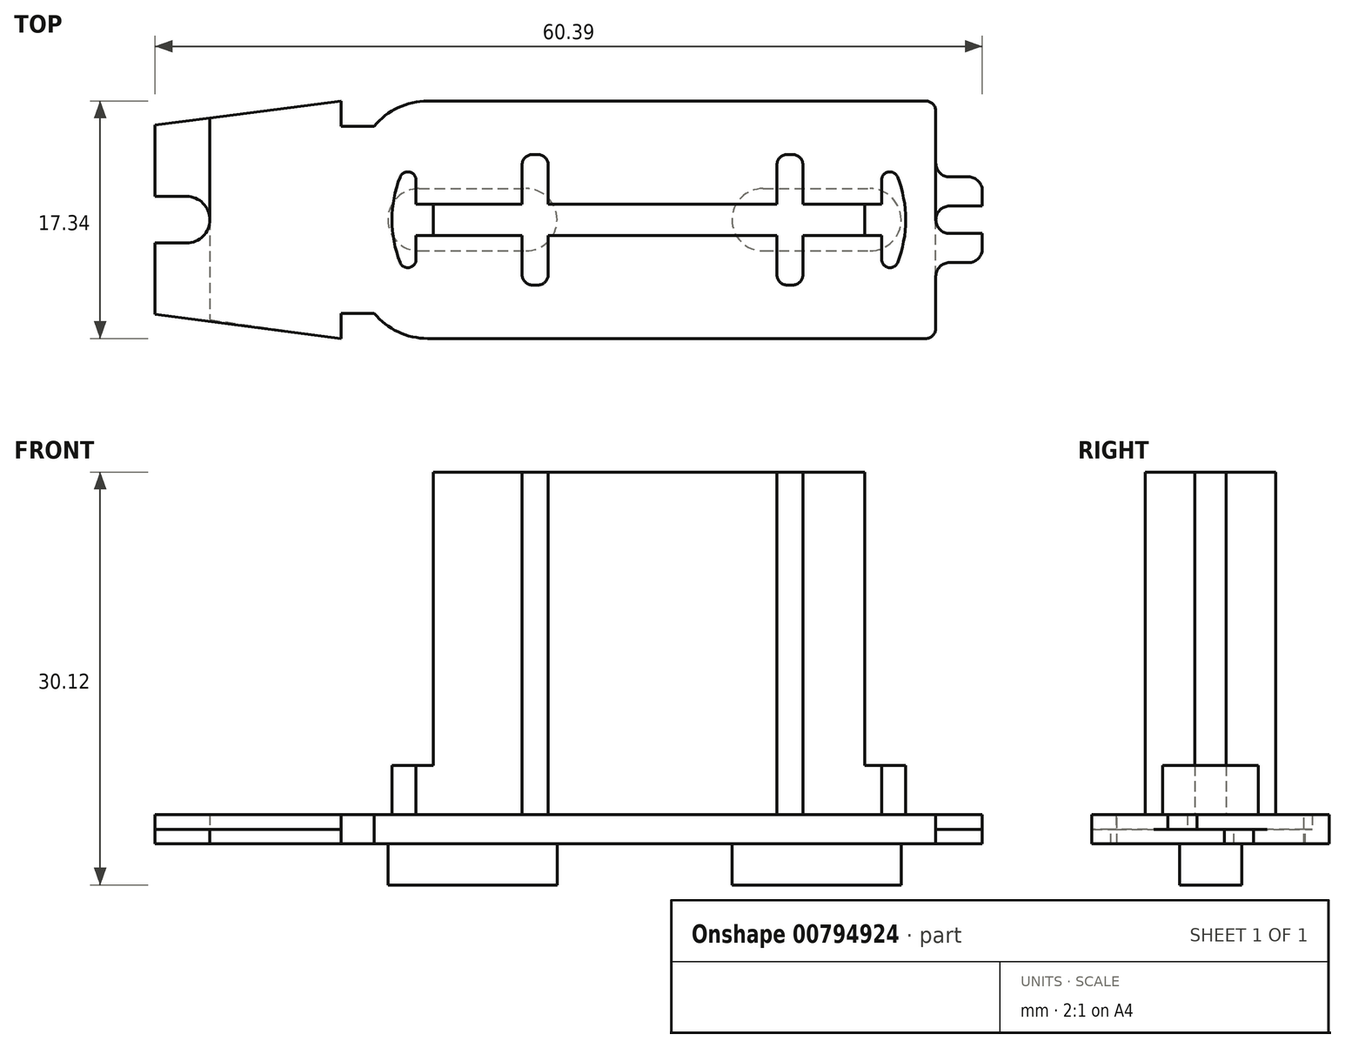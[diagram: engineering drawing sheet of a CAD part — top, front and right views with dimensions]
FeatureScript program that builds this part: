
annotation { "Feature Type Name" : "Feature", "Feature Type Description" : "" }
export const myFeature = defineFeature(function(context is Context, id is Id, definition is map)
    precondition{}
    {
        {
            var Q0;
            Q0=qCreatedBy(makeId("Top.planeOp"),FACE);
            var sketch = newSketch(context, id + "F0", { "sketchPlane" : qUnion([Q0])});
            skLineSegment(sketch, "E0.bottom", {"start": v(-37.1, -8.67) * mm, "end": v(-0.75, -8.67) * mm});
            skLineSegment(sketch, "E0.top", {"start": v(-37.1, 8.67) * mm, "end": v(-0.75, 8.67) * mm});
            skLineSegment(sketch, "E0.right", {"start": v(0, -7.92) * mm, "end": v(0, 0) * mm});
            skLineSegment(sketch, "E1.bottom", {"start": v(1, 3.13) * mm, "end": v(2.39, 3.13) * mm});
            skLineSegment(sketch, "E1.top", {"start": v(1, 1) * mm, "end": v(3.4, 1) * mm});
            skLineSegment(sketch, "E1.right", {"start": v(3.39, 2.12) * mm, "end": v(3.39, 1) * mm});
            skPoint(sketch, "E2.visualSharp", {"position": v(3.39, 3.13) * mm});
            skArc(sketch, "E2.filletArc", {"start": v(3.39, 2.12) * mm, "mid": v(3.1, 2.83) * mm, "end": v(2.39, 3.12) * mm});
            skLineSegment(sketch, "E3.trimOffspring", {"start": v(0, 4.12) * mm, "end": v(0, 7.92) * mm});
            skPoint(sketch, "E4.visualSharp", {"position": v(0, 1) * mm});
            skArc(sketch, "E4.filletArc", {"start": v(1, 1) * mm, "mid": v(0.3, 0.71) * mm, "end": v(0, 0) * mm});
            skPoint(sketch, "E5.visualSharp", {"position": v(0, 3.13) * mm});
            skArc(sketch, "E5.filletArc", {"start": v(0, 4.12) * mm, "mid": v(0.3, 3.42) * mm, "end": v(1, 3.12) * mm});
            skPoint(sketch, "E6.visualSharp", {"position": v(0, 8.67) * mm});
            skArc(sketch, "E6.filletArc", {"start": v(0, 7.92) * mm, "mid": v(-0.22, 8.45) * mm, "end": v(-0.75, 8.67) * mm});
            skPoint(sketch, "E7.visualSharp", {"position": v(0, -8.67) * mm});
            skArc(sketch, "E7.filletArc", {"start": v(-0.75, -8.67) * mm, "mid": v(-0.22, -8.45) * mm, "end": v(0, -7.92) * mm});
            skLineSegment(sketch, "E8.bottom", {"start": v(-41, 6.82) * mm, "end": v(-43.4, 6.82) * mm});
            skLineSegment(sketch, "E8.top", {"start": v(-41, -6.83) * mm, "end": v(-43.4, -6.83) * mm});
            skArc(sketch, "E9", {"start": v(-37.1, 8.67) * mm, "mid": v(-39.26, 8.18) * mm, "end": v(-41, 6.83) * mm});
            skArc(sketch, "E10.MirrorC", {"start": v(-37.1, -8.67) * mm, "mid": v(-39.26, -8.18) * mm, "end": v(-41, -6.82) * mm});
            skLineSegment(sketch, "E11.right", {"start": v(-57, 6.9) * mm, "end": v(-57, 1.7) * mm});
            skLineSegment(sketch, "E12.trimOffspring", {"start": v(-43.4, -6.83) * mm, "end": v(-43.4, -8.66) * mm});
            skLineSegment(sketch, "E13", {"start": v(-43.4, 8.67) * mm, "end": v(-43.4, 6.82) * mm});
            skLineSegment(sketch, "E14", {"start": v(-53, 0) * mm, "end": v(-53, -7.29) * mm});
            skLineSegment(sketch, "E15", {"start": v(-53, -7.29) * mm, "end": v(-43.4, -8.66) * mm});
            skLineSegment(sketch, "E16", {"start": v(-43.4, 8.67) * mm, "end": v(-57, 6.9) * mm});
            skLineSegment(sketch, "E17", {"start": v(-57, 1.7) * mm, "end": v(-54.7, 1.7) * mm});
            skArc(sketch, "E18", {"start": v(-53, 0) * mm, "mid": v(-53.5, 1.2) * mm, "end": v(-54.7, 1.7) * mm});
            skSolve(sketch);
        }
        {
            var Q0;
            Q0 = qSketchRegion(id + "F0", true);
            extrude(context, id + "F1", {"entities" : qUnion([Q0]), "oppositeDirection" : true, "depth" : 1.06 * mm, "offsetDistance" : 25 * mm});
        }
        {
            var Q0;
            Q0=makeQuery(id+"F1.opExtrude","CAP_FACE",FACE,{"disambiguationData":[OSD([sQuery(id+"F0.wireOp",EDGE,"E0.bottom"),sQuery(id+"F0.wireOp",EDGE,"E0.top"),sQuery(id+"F0.wireOp",EDGE,"E0.right"),sQuery(id+"F0.wireOp",EDGE,"E1.bottom"),sQuery(id+"F0.wireOp",EDGE,"E1.top"),sQuery(id+"F0.wireOp",EDGE,"E1.right"),sQuery(id+"F0.wireOp",EDGE,"E2.filletArc"),sQuery(id+"F0.wireOp",EDGE,"E3.trimOffspring"),sQuery(id+"F0.wireOp",EDGE,"E4.filletArc"),sQuery(id+"F0.wireOp",EDGE,"E5.filletArc"),sQuery(id+"F0.wireOp",EDGE,"E6.filletArc"),sQuery(id+"F0.wireOp",EDGE,"E7.filletArc"),sQuery(id+"F0.wireOp",EDGE,"E8.bottom"),sQuery(id+"F0.wireOp",EDGE,"E8.top"),sQuery(id+"F0.wireOp",EDGE,"E9"),sQuery(id+"F0.wireOp",EDGE,"E10.MirrorC"),sQuery(id+"F0.wireOp",EDGE,"E11.right"),sQuery(id+"F0.wireOp",EDGE,"E12.trimOffspring"),sQuery(id+"F0.wireOp",EDGE,"E13"),sQuery(id+"F0.wireOp",EDGE,"E14"),sQuery(id+"F0.wireOp",EDGE,"E15"),sQuery(id+"F0.wireOp",EDGE,"E16"),sQuery(id+"F0.wireOp",EDGE,"E17"),sQuery(id+"F0.wireOp",EDGE,"E18")])],"isStart":true});
            var sketch = newSketch(context, id + "F2", { "sketchPlane" : qUnion([Q0])});
            skArc(sketch, "E19.MirrorCS", {"start": v(-0.75, 8.67) * mm, "mid": v(-0.22, 8.45) * mm, "end": v(0, 7.92) * mm});
            skArc(sketch, "E20.MirrorCS", {"start": v(0, -7.92) * mm, "mid": v(-0.22, -8.45) * mm, "end": v(-0.75, -8.67) * mm});
            skArc(sketch, "E21.MirrorCS", {"start": v(0, -4.12) * mm, "mid": v(0.3, -3.42) * mm, "end": v(1, -3.12) * mm});
            skLineSegment(sketch, "E22.MirrorCS", {"start": v(0, -4.12) * mm, "end": v(0, -7.92) * mm});
            skArc(sketch, "E23.MirrorCS", {"start": v(3.4, -2.12) * mm, "mid": v(3.1, -2.83) * mm, "end": v(2.4, -3.12) * mm});
            skLineSegment(sketch, "E24.MirrorCS", {"start": v(3.4, -2.12) * mm, "end": v(3.4, -1) * mm});
            skLineSegment(sketch, "E25.MirrorCS", {"start": v(1, -1) * mm, "end": v(3.4, -1) * mm});
            skLineSegment(sketch, "E26.MirrorCS", {"start": v(1, -3.12) * mm, "end": v(2.4, -3.12) * mm});
            skLineSegment(sketch, "E27.MirrorCS", {"start": v(-43.4, -8.66) * mm, "end": v(-43.4, -6.83) * mm});
            skLineSegment(sketch, "E28.MirrorCS", {"start": v(-57, -1.7) * mm, "end": v(-54.7, -1.7) * mm});
            skLineSegment(sketch, "E29.MirrorCS", {"start": v(-41, -6.83) * mm, "end": v(-43.4, -6.83) * mm});
            skArc(sketch, "E30.MirrorCS", {"start": v(1, -1) * mm, "mid": v(0.3, -0.71) * mm, "end": v(0, 0) * mm});
            skArc(sketch, "E31.MirrorCS", {"start": v(-37.1, 8.67) * mm, "mid": v(-39.26, 8.18) * mm, "end": v(-41, 6.82) * mm});
            skArc(sketch, "E32.MirrorCS", {"start": v(-37.1, -8.67) * mm, "mid": v(-39.26, -8.18) * mm, "end": v(-41, -6.82) * mm});
            skLineSegment(sketch, "E33.MirrorCS", {"start": v(-41, 6.82) * mm, "end": v(-43.4, 6.82) * mm});
            skLineSegment(sketch, "E34.MirrorCS", {"start": v(-43.4, 6.82) * mm, "end": v(-43.4, 8.67) * mm});
            skArc(sketch, "E35.MirrorCS", {"start": v(-53, 0) * mm, "mid": v(-53.5, -1.2) * mm, "end": v(-54.7, -1.7) * mm});
            skLineSegment(sketch, "E36.MirrorCS", {"start": v(-53, 0) * mm, "end": v(-53, 7.42) * mm});
            skLineSegment(sketch, "E37.MirrorCS", {"start": v(0, 7.91) * mm, "end": v(0, 0) * mm});
            skLineSegment(sketch, "E38.MirrorCS", {"start": v(-37.1, -8.67) * mm, "end": v(-0.75, -8.67) * mm});
            skLineSegment(sketch, "E39.MirrorCS", {"start": v(-37.1, 8.67) * mm, "end": v(-0.75, 8.67) * mm});
            skLineSegment(sketch, "E40.MirrorCS", {"start": v(-43.4, -8.67) * mm, "end": v(-57, -6.9) * mm});
            skLineSegment(sketch, "E41.MirrorCS", {"start": v(-57, -6.9) * mm, "end": v(-57, -1.7) * mm});
            skLineSegment(sketch, "E42.MirrorCS", {"start": v(-53, 7.42) * mm, "end": v(-43.4, 8.67) * mm});
            skSolve(sketch);
        }
        {
            var Q0;
            Q0 = qSketchRegion(id + "F2", true);
            extrude(context, id + "F3", {"entities" : qUnion([Q0]), "operationType" : NewBodyOperationType.ADD, "depth" : 1.06 * mm, "offsetDistance" : 25 * mm});
        }
        {
            var Q0;
            Q0=makeQuery(id+"F1.opExtrude","CAP_FACE",FACE,{"disambiguationData":[OSD([sQuery(id+"F0.wireOp",EDGE,"E0.bottom"),sQuery(id+"F0.wireOp",EDGE,"E0.top"),sQuery(id+"F0.wireOp",EDGE,"E0.right"),sQuery(id+"F0.wireOp",EDGE,"E1.bottom"),sQuery(id+"F0.wireOp",EDGE,"E1.top"),sQuery(id+"F0.wireOp",EDGE,"E1.right"),sQuery(id+"F0.wireOp",EDGE,"E2.filletArc"),sQuery(id+"F0.wireOp",EDGE,"E3.trimOffspring"),sQuery(id+"F0.wireOp",EDGE,"E4.filletArc"),sQuery(id+"F0.wireOp",EDGE,"E5.filletArc"),sQuery(id+"F0.wireOp",EDGE,"E6.filletArc"),sQuery(id+"F0.wireOp",EDGE,"E7.filletArc"),sQuery(id+"F0.wireOp",EDGE,"E8.bottom"),sQuery(id+"F0.wireOp",EDGE,"E8.top"),sQuery(id+"F0.wireOp",EDGE,"E9"),sQuery(id+"F0.wireOp",EDGE,"E10.MirrorC"),sQuery(id+"F0.wireOp",EDGE,"E11.right"),sQuery(id+"F0.wireOp",EDGE,"E12.trimOffspring"),sQuery(id+"F0.wireOp",EDGE,"E13"),sQuery(id+"F0.wireOp",EDGE,"E14"),sQuery(id+"F0.wireOp",EDGE,"E15"),sQuery(id+"F0.wireOp",EDGE,"E16"),sQuery(id+"F0.wireOp",EDGE,"E17"),sQuery(id+"F0.wireOp",EDGE,"E18")])],"isStart":false});
            var sketch = newSketch(context, id + "F4", { "sketchPlane" : qUnion([Q0])});
            skLineSegment(sketch, "E43.bottom", {"start": v(-37.72, 2.28) * mm, "end": v(-29.93, 2.28) * mm});
            skLineSegment(sketch, "E43.top", {"start": v(-37.72, -2.27) * mm, "end": v(-29.93, -2.27) * mm});
            skLineSegment(sketch, "E44.bottom", {"start": v(-12.6, 2.28) * mm, "end": v(-4.8, 2.28) * mm});
            skLineSegment(sketch, "E44.top", {"start": v(-12.6, -2.27) * mm, "end": v(-4.8, -2.27) * mm});
            skArc(sketch, "E45", {"start": v(-37.72, 2.27) * mm, "mid": v(-40, 0) * mm, "end": v(-37.72, -2.28) * mm});
            skArc(sketch, "E46", {"start": v(-29.93, -2.28) * mm, "mid": v(-27.65, 0) * mm, "end": v(-29.93, 2.27) * mm});
            skArc(sketch, "E47", {"start": v(-12.6, 2.27) * mm, "mid": v(-14.88, 0) * mm, "end": v(-12.6, -2.28) * mm});
            skArc(sketch, "E48", {"start": v(-4.8, -2.27) * mm, "mid": v(-2.53, 0) * mm, "end": v(-4.8, 2.28) * mm});
            skSolve(sketch);
        }
        {
            var Q0;
            Q0 = qSketchRegion(id + "F4", true);
            extrude(context, id + "F5", {"entities" : qUnion([Q0]), "operationType" : NewBodyOperationType.ADD, "depth" : 3 * mm, "offsetDistance" : 25 * mm});
        }
        {
            var Q0;
            Q0=makeQuery(id+"F3.opExtrude","CAP_FACE",FACE,{"disambiguationData":[OSD([sQuery(id+"F2.wireOp",EDGE,"E19.MirrorCS"),sQuery(id+"F2.wireOp",EDGE,"E20.MirrorCS"),sQuery(id+"F2.wireOp",EDGE,"E21.MirrorCS"),sQuery(id+"F2.wireOp",EDGE,"E22.MirrorCS"),sQuery(id+"F2.wireOp",EDGE,"E23.MirrorCS"),sQuery(id+"F2.wireOp",EDGE,"E24.MirrorCS"),sQuery(id+"F2.wireOp",EDGE,"E25.MirrorCS"),sQuery(id+"F2.wireOp",EDGE,"E26.MirrorCS"),sQuery(id+"F2.wireOp",EDGE,"E27.MirrorCS"),sQuery(id+"F2.wireOp",EDGE,"E28.MirrorCS"),sQuery(id+"F2.wireOp",EDGE,"E29.MirrorCS"),sQuery(id+"F2.wireOp",EDGE,"E30.MirrorCS"),sQuery(id+"F2.wireOp",EDGE,"E31.MirrorCS"),sQuery(id+"F2.wireOp",EDGE,"E32.MirrorCS"),sQuery(id+"F2.wireOp",EDGE,"E33.MirrorCS"),sQuery(id+"F2.wireOp",EDGE,"E34.MirrorCS"),sQuery(id+"F2.wireOp",EDGE,"E35.MirrorCS"),sQuery(id+"F2.wireOp",EDGE,"E36.MirrorCS"),sQuery(id+"F2.wireOp",EDGE,"E37.MirrorCS"),sQuery(id+"F2.wireOp",EDGE,"E38.MirrorCS"),sQuery(id+"F2.wireOp",EDGE,"E39.MirrorCS"),sQuery(id+"F2.wireOp",EDGE,"E40.MirrorCS"),sQuery(id+"F2.wireOp",EDGE,"E41.MirrorCS"),sQuery(id+"F2.wireOp",EDGE,"E42.MirrorCS")])],"isStart":false});
            var sketch = newSketch(context, id + "F6", { "sketchPlane" : qUnion([Q0])});
            skLineSegment(sketch, "E49.bottom", {"start": v(-36.7, 1.15) * mm, "end": v(-30.2, 1.15) * mm});
            skLineSegment(sketch, "E49.top", {"start": v(-36.7, -1.15) * mm, "end": v(-30.2, -1.15) * mm});
            skLineSegment(sketch, "E49.left", {"start": v(-36.7, 1.15) * mm, "end": v(-36.7, -1.15) * mm});
            skLineSegment(sketch, "E49.right", {"start": v(-5.2, 1.15) * mm, "end": v(-5.2, -1.15) * mm});
            skLineSegment(sketch, "E50.bottom", {"start": v(-29.45, 4.76) * mm, "end": v(-29.05, 4.76) * mm});
            skLineSegment(sketch, "E50.top", {"start": v(-29.45, -4.76) * mm, "end": v(-29.05, -4.76) * mm});
            skLineSegment(sketch, "E50.left", {"start": v(-30.2, 4.01) * mm, "end": v(-30.2, 1.15) * mm});
            skLineSegment(sketch, "E50.right", {"start": v(-28.3, 4.01) * mm, "end": v(-28.3, 1.15) * mm});
            skLineSegment(sketch, "E51.bottom", {"start": v(-10.85, 4.76) * mm, "end": v(-10.45, 4.76) * mm});
            skLineSegment(sketch, "E51.top", {"start": v(-10.85, -4.76) * mm, "end": v(-10.45, -4.76) * mm});
            skLineSegment(sketch, "E51.left", {"start": v(-11.6, 4.01) * mm, "end": v(-11.6, 1.15) * mm});
            skLineSegment(sketch, "E51.right", {"start": v(-9.7, 4.01) * mm, "end": v(-9.7, 1.15) * mm});
            skLineSegment(sketch, "E52.trimOffspring", {"start": v(-30.2, -1.15) * mm, "end": v(-30.2, -4.01) * mm});
            skLineSegment(sketch, "E53.trimOffspring", {"start": v(-28.3, -1.15) * mm, "end": v(-28.3, -4.01) * mm});
            skLineSegment(sketch, "E54.trimOffspring", {"start": v(-11.6, -1.15) * mm, "end": v(-11.6, -4.01) * mm});
            skLineSegment(sketch, "E55.trimOffspring", {"start": v(-9.7, -1.15) * mm, "end": v(-9.7, -4.01) * mm});
            skLineSegment(sketch, "E56.trimOffspring", {"start": v(-9.7, -1.15) * mm, "end": v(-5.2, -1.15) * mm});
            skLineSegment(sketch, "E57.trimOffspring", {"start": v(-9.7, 1.15) * mm, "end": v(-5.2, 1.15) * mm});
            skLineSegment(sketch, "E58.trimOffspring", {"start": v(-28.3, 1.15) * mm, "end": v(-11.6, 1.15) * mm});
            skLineSegment(sketch, "E59.trimOffspring", {"start": v(-28.3, -1.15) * mm, "end": v(-11.6, -1.15) * mm});
            skPoint(sketch, "E60.visualSharp", {"position": v(-30.2, 4.76) * mm});
            skArc(sketch, "E60.filletArc", {"start": v(-29.45, 4.76) * mm, "mid": v(-29.98, 4.54) * mm, "end": v(-30.2, 4.01) * mm});
            skPoint(sketch, "E61.visualSharp", {"position": v(-28.3, 4.76) * mm});
            skArc(sketch, "E61.filletArc", {"start": v(-28.3, 4.01) * mm, "mid": v(-28.52, 4.54) * mm, "end": v(-29.05, 4.76) * mm});
            skPoint(sketch, "E62.visualSharp", {"position": v(-11.6, 4.76) * mm});
            skArc(sketch, "E62.filletArc", {"start": v(-10.85, 4.76) * mm, "mid": v(-11.38, 4.54) * mm, "end": v(-11.6, 4.01) * mm});
            skPoint(sketch, "E63.visualSharp", {"position": v(-9.7, 4.76) * mm});
            skArc(sketch, "E63.filletArc", {"start": v(-9.7, 4.01) * mm, "mid": v(-9.92, 4.54) * mm, "end": v(-10.45, 4.76) * mm});
            skPoint(sketch, "E64.visualSharp", {"position": v(-9.7, -4.76) * mm});
            skArc(sketch, "E64.filletArc", {"start": v(-10.45, -4.76) * mm, "mid": v(-9.92, -4.54) * mm, "end": v(-9.7, -4.01) * mm});
            skPoint(sketch, "E65.visualSharp", {"position": v(-11.6, -4.76) * mm});
            skArc(sketch, "E65.filletArc", {"start": v(-11.6, -4.01) * mm, "mid": v(-11.38, -4.54) * mm, "end": v(-10.85, -4.76) * mm});
            skPoint(sketch, "E66.visualSharp", {"position": v(-28.3, -4.76) * mm});
            skArc(sketch, "E66.filletArc", {"start": v(-29.05, -4.76) * mm, "mid": v(-28.52, -4.54) * mm, "end": v(-28.3, -4.01) * mm});
            skPoint(sketch, "E67.visualSharp", {"position": v(-30.2, -4.76) * mm});
            skArc(sketch, "E67.filletArc", {"start": v(-30.2, -4.01) * mm, "mid": v(-29.98, -4.54) * mm, "end": v(-29.45, -4.76) * mm});
            skSolve(sketch);
        }
        {
            var Q0;
            Q0 = qSketchRegion(id + "F6", true);
            extrude(context, id + "F7", {"entities" : qUnion([Q0]), "operationType" : NewBodyOperationType.ADD, "depth" : 25 * mm, "offsetDistance" : 25 * mm});
        }
        {
            var Q0;
            Q0=makeQuery(id+"F3.opExtrude","CAP_FACE",FACE,{"disambiguationData":[OSD([sQuery(id+"F2.wireOp",EDGE,"E19.MirrorCS"),sQuery(id+"F2.wireOp",EDGE,"E20.MirrorCS"),sQuery(id+"F2.wireOp",EDGE,"E21.MirrorCS"),sQuery(id+"F2.wireOp",EDGE,"E22.MirrorCS"),sQuery(id+"F2.wireOp",EDGE,"E23.MirrorCS"),sQuery(id+"F2.wireOp",EDGE,"E24.MirrorCS"),sQuery(id+"F2.wireOp",EDGE,"E25.MirrorCS"),sQuery(id+"F2.wireOp",EDGE,"E26.MirrorCS"),sQuery(id+"F2.wireOp",EDGE,"E27.MirrorCS"),sQuery(id+"F2.wireOp",EDGE,"E28.MirrorCS"),sQuery(id+"F2.wireOp",EDGE,"E29.MirrorCS"),sQuery(id+"F2.wireOp",EDGE,"E30.MirrorCS"),sQuery(id+"F2.wireOp",EDGE,"E31.MirrorCS"),sQuery(id+"F2.wireOp",EDGE,"E32.MirrorCS"),sQuery(id+"F2.wireOp",EDGE,"E33.MirrorCS"),sQuery(id+"F2.wireOp",EDGE,"E34.MirrorCS"),sQuery(id+"F2.wireOp",EDGE,"E35.MirrorCS"),sQuery(id+"F2.wireOp",EDGE,"E36.MirrorCS"),sQuery(id+"F2.wireOp",EDGE,"E37.MirrorCS"),sQuery(id+"F2.wireOp",EDGE,"E38.MirrorCS"),sQuery(id+"F2.wireOp",EDGE,"E39.MirrorCS"),sQuery(id+"F2.wireOp",EDGE,"E40.MirrorCS"),sQuery(id+"F2.wireOp",EDGE,"E41.MirrorCS"),sQuery(id+"F2.wireOp",EDGE,"E42.MirrorCS")])],"isStart":false});
            var sketch = newSketch(context, id + "F8", { "sketchPlane" : qUnion([Q0])});
            skLineSegment(sketch, "E68.0", {"start": v(-37.95, 2.9) * mm, "end": v(-37.95, 1.15) * mm});
            skLineSegment(sketch, "E69", {"start": v(-37.95, -1.15) * mm, "end": v(-36.7, -1.15) * mm});
            skLineSegment(sketch, "E70", {"start": v(-36.7, -1.15) * mm, "end": v(-36.7, 1.15) * mm});
            skLineSegment(sketch, "E71", {"start": v(-36.7, 1.15) * mm, "end": v(-37.95, 1.15) * mm});
            skLineSegment(sketch, "E72.trimOffspring", {"start": v(-37.95, -1.15) * mm, "end": v(-37.95, -2.9) * mm});
            skArc(sketch, "E73", {"start": v(-37.95, 2.9) * mm, "mid": v(-38.44, 3.49) * mm, "end": v(-39.1, 3.12) * mm});
            skPoint(sketch, "E73.first.point", {"position": v(-37.95, 2.9) * mm});
            skArc(sketch, "E74.MirrorC", {"start": v(-37.95, -2.9) * mm, "mid": v(-38.44, -3.49) * mm, "end": v(-39.1, -3.12) * mm});
            skLineSegment(sketch, "E75", {"start": v(-39.7, -4.36) * mm, "end": v(-39.7, 4.16) * mm, "construction": true});
            skArc(sketch, "E76", {"start": v(-39.1, 3.12) * mm, "mid": v(-39.7, 0) * mm, "end": v(-39.1, -3.12) * mm});
            skPoint(sketch, "E76.first.point", {"position": v(-39.1, 3.12) * mm});
            skPoint(sketch, "E76.second.point", {"position": v(-39.7, 0) * mm});
            skPoint(sketch, "E76.third.point", {"position": v(-39.1, -3.12) * mm});
            skLineSegment(sketch, "E77", {"start": v(-36.7, 0) * mm, "end": v(-5.2, 0) * mm, "construction": true});
            skLineSegment(sketch, "E78", {"start": v(-20.95, -8.67) * mm, "end": v(-20.95, 8.67) * mm, "construction": true});
            skLineSegment(sketch, "E79.MirrorCS", {"start": v(-3.95, -1.15) * mm, "end": v(-5.2, -1.15) * mm});
            skLineSegment(sketch, "E80.MirrorCS", {"start": v(-5.2, 1.15) * mm, "end": v(-3.95, 1.15) * mm});
            skLineSegment(sketch, "E81.MirrorCS", {"start": v(-5.2, -1.15) * mm, "end": v(-5.2, 1.15) * mm});
            skArc(sketch, "E82.MirrorCS", {"start": v(-3.95, 2.9) * mm, "mid": v(-3.46, 3.49) * mm, "end": v(-2.8, 3.12) * mm});
            skArc(sketch, "E83.MirrorCS", {"start": v(-3.95, -2.9) * mm, "mid": v(-3.46, -3.49) * mm, "end": v(-2.8, -3.12) * mm});
            skPoint(sketch, "E84.MirrorP", {"position": v(-2.2, 0) * mm});
            skPoint(sketch, "E85.MirrorP", {"position": v(-3.95, 2.9) * mm});
            skLineSegment(sketch, "E86.MirrorCS", {"start": v(-3.95, 2.9) * mm, "end": v(-3.95, 1.15) * mm});
            skLineSegment(sketch, "E87.MirrorCS", {"start": v(-3.95, -1.15) * mm, "end": v(-3.95, -2.9) * mm});
            skPoint(sketch, "E88.MirrorP", {"position": v(-2.8, 3.12) * mm});
            skArc(sketch, "E89.MirrorCS", {"start": v(-2.8, 3.12) * mm, "mid": v(-2.2, 0) * mm, "end": v(-2.8, -3.12) * mm});
            skPoint(sketch, "E90.MirrorP", {"position": v(-2.8, -3.12) * mm});
            skSolve(sketch);
        }
        {
            var Q0;
            Q0 = qSketchRegion(id + "F8", true);
            extrude(context, id + "F9", {"entities" : qUnion([Q0]), "operationType" : NewBodyOperationType.ADD, "depth" : 3.6 * mm, "offsetDistance" : 25 * mm});
        }
    });
